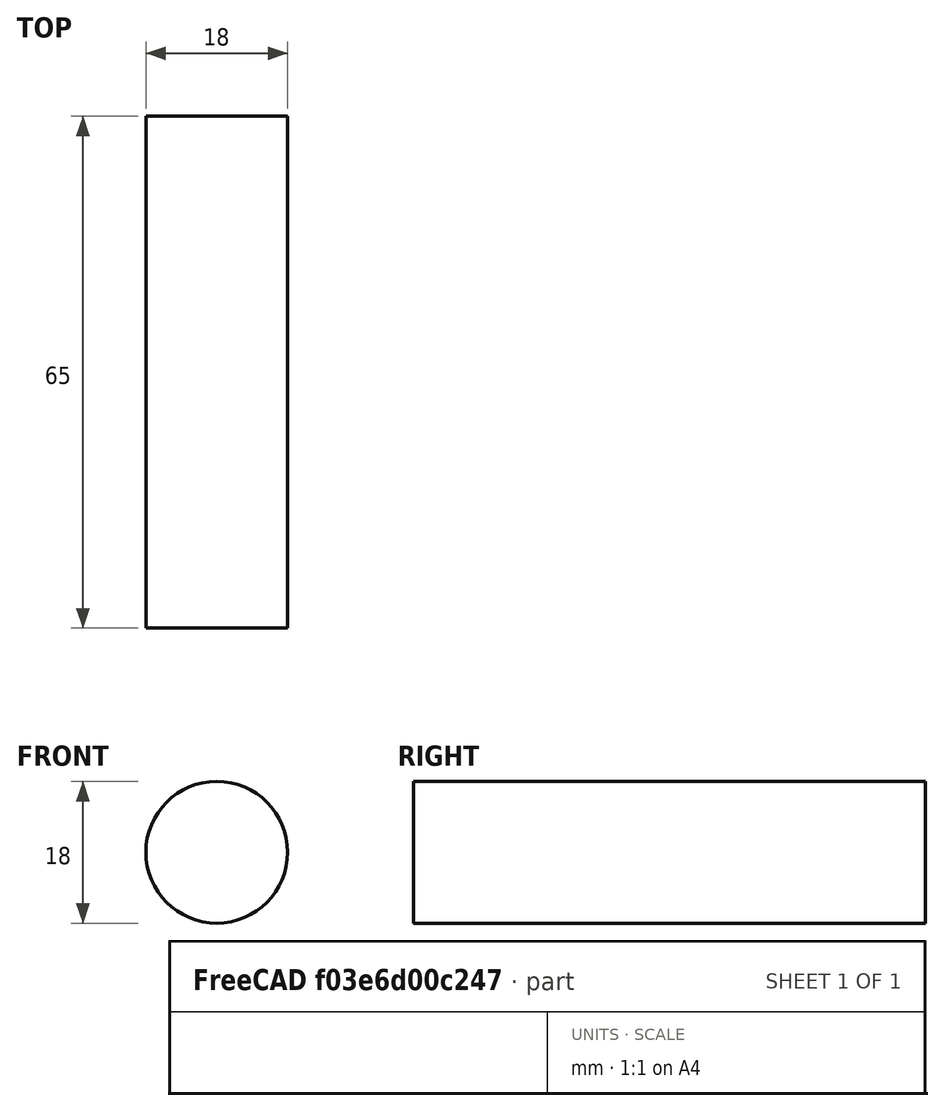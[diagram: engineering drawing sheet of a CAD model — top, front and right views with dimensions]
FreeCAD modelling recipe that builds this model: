
FCSTD DOCUMENT  (FreeCAD 1.0R39319 (Git))
Label: 18650
License: All rights reserved
LicenseURL: http://en.wikipedia.org/wiki/All_rights_reserved
objects: Sketcher::SketchObject×1, PartDesign::Pad×1, PartDesign::Body×1, App::Part×1
note: 6 computed .brp shape members not serialized (recipe doc carries the construction recipe); baked Part::Feature solids carry a one-line shape summary decoded from their .brp

FEATURE [Sketcher::SketchObject] Sketch
  ArcFitTolerance = 1e-06
  AttachmentSupport = -> [XZ_Plane001]
  FullyConstrained = true
  MakeInternals = false
  MapMode = 5
  Placement = pos=(0,0,0) rot=(1,0,0;1.5708rad)
  sketch-geometry (1):
    g0: Circle CenterX=0 CenterY=0 CenterZ=0 NormalX=0 NormalY=0 NormalZ=1 AngleXU=0 Radius=9
  constraints (2):
    c: Coincident(g0,g-1)
    c: Diameter(g0) = 18
FEATURE [PartDesign::Pad] Pad
  Direction = (0,-1,2e-16)
  Length = 65
  Length2 = 10
  Placement = pos=(0,0,0) rot=(1,0,0;1.5708rad)
  Profile = -> Sketch
  ReferenceAxis = -> Sketch [N_Axis]
  Refine = true
  Suppressed = false
  Type = 0
FEATURE [PartDesign::Body] Body  label="18650001"
  AllowCompound = false
  Group = -> [Sketch,Pad]
  Origin = -> Origin001
  Tip = -> Pad
FEATURE [App::Part] Part  label="18650"
  Group = -> [Body]
  Origin = -> Origin
